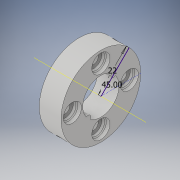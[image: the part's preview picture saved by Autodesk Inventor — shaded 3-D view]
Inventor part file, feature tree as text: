
AUTODESK INVENTOR PART (.ipt)
format: ipt  version: 2019 (Build 230136000, 136)  size: 194,560 bytes
history: native  units: in
note: dims shown in document units (in); Inventor stores cm internally (conversion verified against a paired STEP export)
features: sketch x6, extrude x5, plane x2, thread x1, mirror x1, chamfer x1, pattern_circular x1
ambient origin geometry x8: Origin, YZ Plane, XZ Plane, XY Plane, X Axis, Y Axis, Z Axis, Center Point
bodies: Solid1 (feature_tree)
feature tree (17):
  extrude  "Extrusion1"  Depth=1.7323in
  extrude  "Extrusion3"  Depth=0.4724in
  extrude  "Extrusion4"  Depth=1.1811in TaperAngle=0.0deg
  sketch  "Sketch6"  dims[d13=1.5748in d14=360.0deg d16=0.3937in d17=45.0deg]
  plane  "Work Plane1"
  extrude  "Extrusion5"  Depth=0.3937in
  plane  "Work Plane2"
  thread  "Thread1"  [1 undecoded]
  mirror  "Mirror1"
  extrude  "Extrusion6"  TaperAngle=45.0deg  [1 undecoded]
  chamfer  "Chamfer2"  Distance=0.1575in
  pattern_circular  "Circular Pattern1"  [2 undecoded]
  sketch  "Sketch2"  dims[d3=0.7874in d4=1.7323in]
  sketch  "Sketch4"  dims[d5=0.4724in d6=0.0in d9=1.2402in]
  sketch  "Sketch5"  dims[d10=0.2008in d11=1.1811in d12=0.0in]
  sketch  "Sketch7"  dims[d18=0.1181in d19=45.0deg]
  sketch  "Sketch8"  dims[d20=0.3543in d21=0.1575in d22=0.0in d23=0.8661in d24=45.0deg d25=0.2047in d26=0.3937in d27=0.0in d28=0.3937in d29=0.0in d33=0.3937in d34=0.0787in d35=0.0in d36=0.0197in d37=0.0787in d38=0.2542in]
note: 4 required parameter values undecoded (feature->parameter linkage not recoverable at this tier; creation-order binding heuristic only, values carry confidence <= 0.55)
